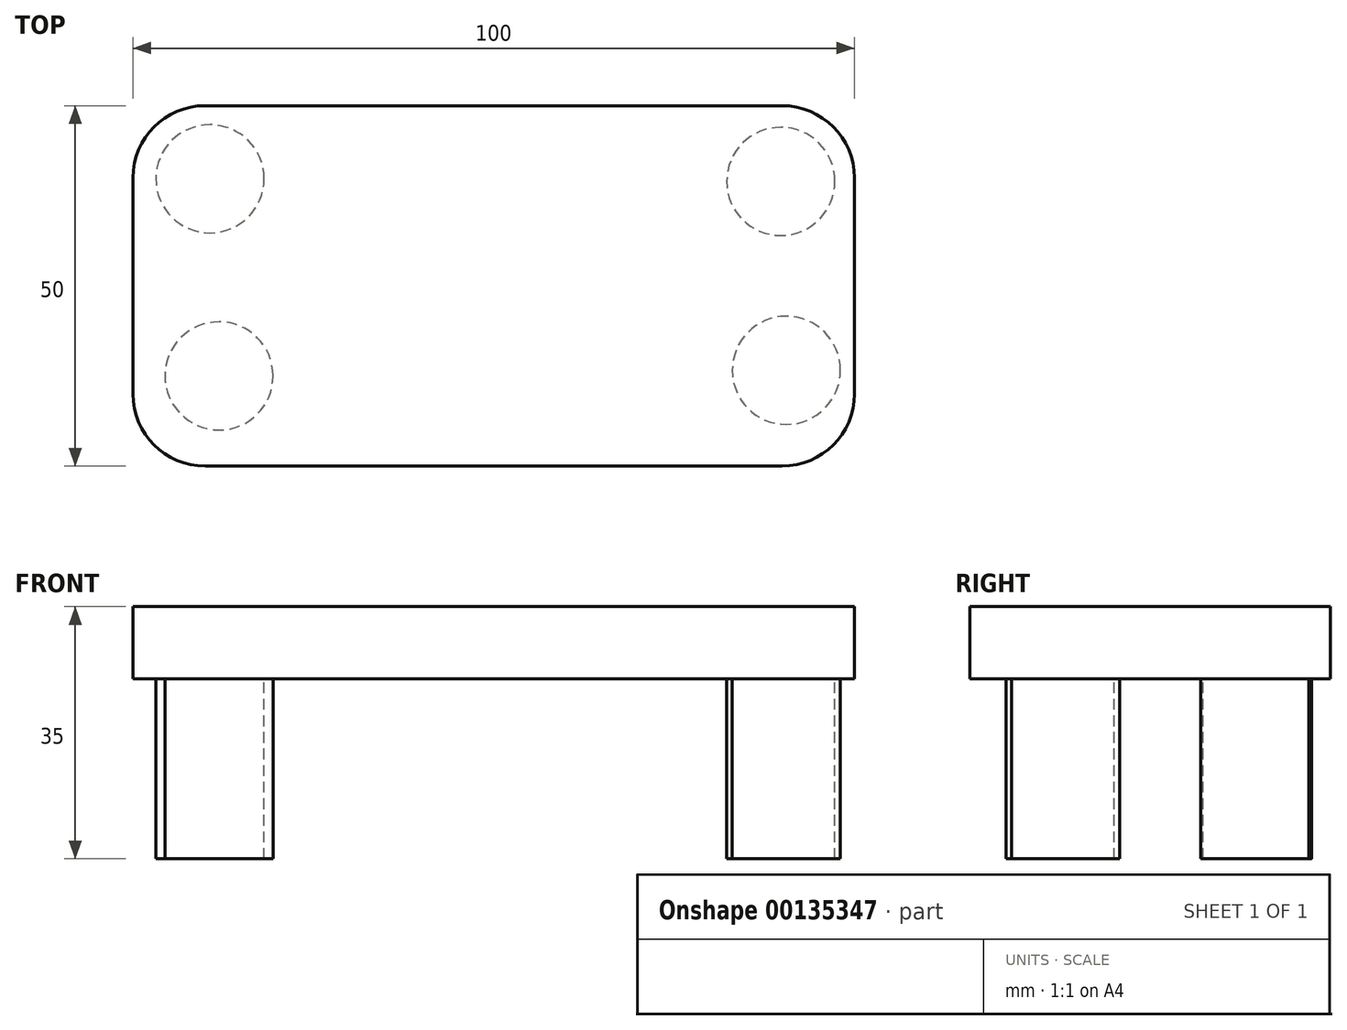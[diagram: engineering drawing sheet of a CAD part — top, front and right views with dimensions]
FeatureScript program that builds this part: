
annotation { "Feature Type Name" : "Feature", "Feature Type Description" : "" }
export const myFeature = defineFeature(function(context is Context, id is Id, definition is map)
    precondition{}
    {
        {
            var Q0;
            Q0=qCreatedBy(makeId("Top.planeOp"),FACE);
            var sketch = newSketch(context, id + "F0", { "sketchPlane" : qUnion([Q0])});
            skLineSegment(sketch, "E0.bottom", {"start": v(-40, 25) * mm, "end": v(40, 25) * mm});
            skLineSegment(sketch, "E0.top", {"start": v(-40, -25) * mm, "end": v(40, -25) * mm});
            skLineSegment(sketch, "E0.left", {"start": v(-50, 15) * mm, "end": v(-50, -15) * mm});
            skLineSegment(sketch, "E0.right", {"start": v(50, 15) * mm, "end": v(50, -15) * mm});
            skPoint(sketch, "E0.middle", {"position": v(0, 0) * mm});
            skPoint(sketch, "E1.visualSharp", {"position": v(-50, 25) * mm});
            skArc(sketch, "E1.filletArc", {"start": v(-40, 25) * mm, "mid": v(-47.07, 22.07) * mm, "end": v(-50, 15) * mm});
            skPoint(sketch, "E2.visualSharp", {"position": v(-50, -25) * mm});
            skArc(sketch, "E2.filletArc", {"start": v(-50, -15) * mm, "mid": v(-47.07, -22.07) * mm, "end": v(-40, -25) * mm});
            skPoint(sketch, "E3.visualSharp", {"position": v(50, -25) * mm});
            skArc(sketch, "E3.filletArc", {"start": v(40, -25) * mm, "mid": v(47.07, -22.07) * mm, "end": v(50, -15) * mm});
            skPoint(sketch, "E4.visualSharp", {"position": v(50, 25) * mm});
            skArc(sketch, "E4.filletArc", {"start": v(50, 15) * mm, "mid": v(47.07, 22.07) * mm, "end": v(40, 25) * mm});
            skSolve(sketch);
        }
        {
            var Q0;
            Q0 = qSketchRegion(id + "F0", true);
            extrude(context, id + "F1", {"entities" : qUnion([Q0]), "depth" : 10 * mm});
        }
        {
            var Q0;
            Q0=qCreatedBy(makeId("Top.planeOp"),FACE);
            var sketch = newSketch(context, id + "F2", { "sketchPlane" : qUnion([Q0])});
            skCircle(sketch, "E5", {"center": v(-39.33, 14.86) * mm, "radius": 7.5 * mm});
            skCircle(sketch, "E6", {"center": v(-38.09, -12.49) * mm, "radius": 7.5 * mm});
            skCircle(sketch, "E7", {"center": v(39.8, 14.5) * mm, "radius": 7.5 * mm});
            skCircle(sketch, "E8", {"center": v(40.57, -11.72) * mm, "radius": 7.5 * mm});
            skSolve(sketch);
        }
        {
            var Q0;
            Q0 = qSketchRegion(id + "F2", true);
            extrude(context, id + "F3", {"entities" : qUnion([Q0]), "operationType" : NewBodyOperationType.ADD, "oppositeDirection" : true, "depth" : 25 * mm});
        }
    });
